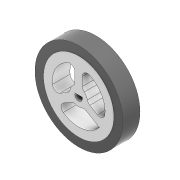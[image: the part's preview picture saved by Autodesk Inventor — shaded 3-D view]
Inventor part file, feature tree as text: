
AUTODESK INVENTOR PART (.ipt)
format: ipt  version: 2022 (Build 260153000, 153)  size: 175,616 bytes
history: native  units: mm
features: extrude x5, sketch x5, fillet x1, mirror x1
ambient origin geometry x8: Origin, YZ Plane, XZ Plane, XY Plane, X Axis, Y Axis, Z Axis, Center Point
bodies: Solid1 (feature_tree)
feature tree (12):
  extrude  "Extrusion1"  Depth=7.0mm TaperAngle=0.0deg
  extrude  "Extrusion2"  Depth=7.0mm
  fillet  "Fillet1"  Radius=3.0mm
  extrude  "Extrusion4"  TaperAngle=0.0deg  [1 undecoded]
  extrude  "Extrusion3"  TaperAngle=0.0deg  [1 undecoded]
  extrude  "Extrusion5"  Depth=2.0mm
  mirror  "Mirror1"
  sketch  "Sketch1"  dims[d0=35.0mm d1=7.0mm d2=0.0mm]
  sketch  "Sketch2"  dims[d3=21.0mm d4=7.0mm d5=3.0mm]
  sketch  "Sketch3"  dims[d6=30.0mm d8=360.0deg d10=0.0mm d11=0.0mm]
  sketch  "Sketch4"  dims[d12=2.0mm d15=0.0mm d16=0.0mm]
  sketch  "Sketch5"  dims[d17=3.0mm d19=2.0mm d20=2.0mm d21=0.0mm d22=28.0mm d23=0.1mm d24=0.0mm]
note: 2 required parameter values undecoded (feature->parameter linkage not recoverable at this tier; creation-order binding heuristic only, values carry confidence <= 0.55)
